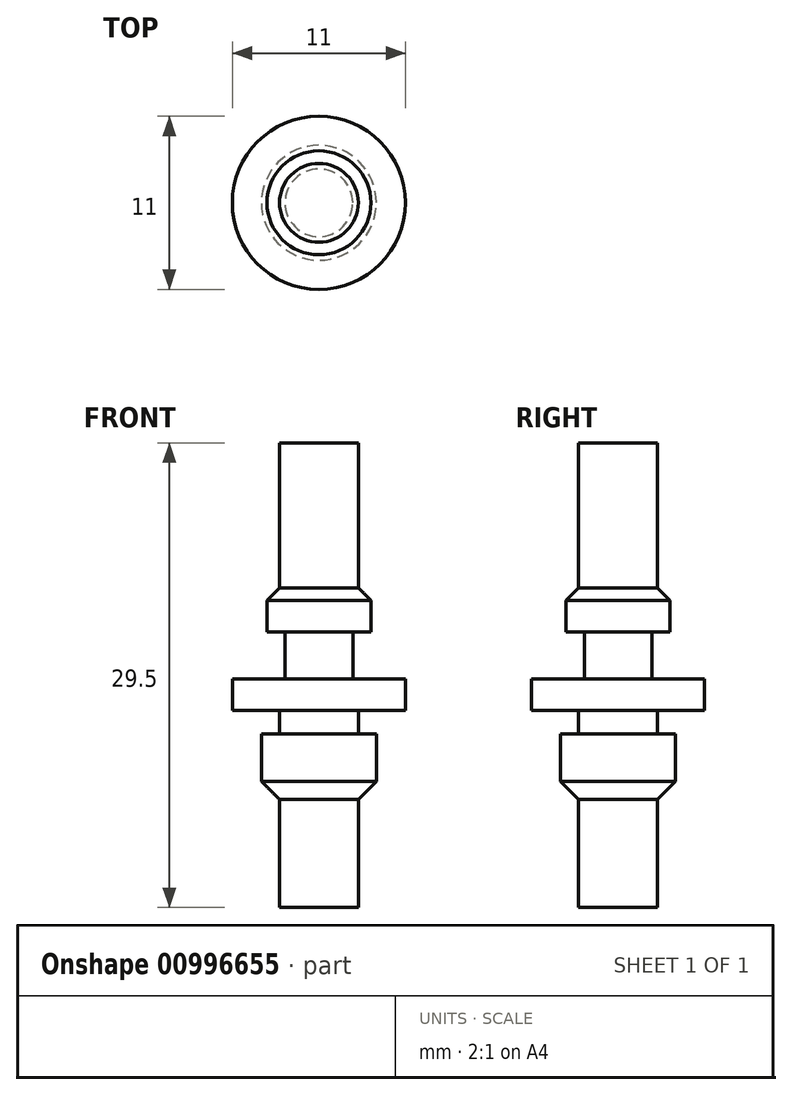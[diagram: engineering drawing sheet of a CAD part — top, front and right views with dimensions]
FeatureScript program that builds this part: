
annotation { "Feature Type Name" : "Feature", "Feature Type Description" : "" }
export const myFeature = defineFeature(function(context is Context, id is Id, definition is map)
    precondition{}
    {
        {
            var Q0;
            Q0=qCreatedBy(makeId("Top.planeOp"),FACE);
            var sketch = newSketch(context, id + "F0", { "sketchPlane" : qUnion([Q0])});
            skCircle(sketch, "E0", {"center": v(0, 0) * mm, "radius": 5.5 * mm});
            skSolve(sketch);
        }
        {
            var Q0;
            Q0 = qSketchRegion(id + "F0", true);
            extrude(context, id + "F1", {"entities" : qUnion([Q0]), "depth" : 2 * mm, "offsetDistance" : 25 * mm});
        }
        {
            var Q0;
            Q0=makeQuery(id+"F1.opExtrude","CAP_FACE",FACE,{"disambiguationData":[OSD([sQuery(id+"F0.wireOp",EDGE,"E0")])],"isStart":false});
            var sketch = newSketch(context, id + "F2", { "sketchPlane" : qUnion([Q0])});
            skCircle(sketch, "E1", {"center": v(0, 0) * mm, "radius": 2.15 * mm});
            skSolve(sketch);
        }
        {
            var Q0;
            Q0 = qSketchRegion(id + "F2", true);
            extrude(context, id + "F3", {"entities" : qUnion([Q0]), "operationType" : NewBodyOperationType.ADD, "depth" : 3 * mm, "offsetDistance" : 25 * mm});
        }
        {
            var Q0;
            Q0=makeQuery(id+"F3.opExtrude","CAP_FACE",FACE,{"disambiguationData":[OSD([sQuery(id+"F2.wireOp",EDGE,"E1")])],"isStart":false});
            var sketch = newSketch(context, id + "F4", { "sketchPlane" : qUnion([Q0])});
            skCircle(sketch, "E2", {"center": v(0, 0) * mm, "radius": 3.3 * mm});
            skSolve(sketch);
        }
        {
            var Q0;
            Q0 = qSketchRegion(id + "F4", true);
            extrude(context, id + "F5", {"entities" : qUnion([Q0]), "operationType" : NewBodyOperationType.ADD, "depth" : 12 * mm, "offsetDistance" : 25 * mm});
        }
        {
            var Q0;
            Q0=makeQuery(id+"F5.opExtrude","CAP_FACE",FACE,{"disambiguationData":[OSD([sQuery(id+"F4.wireOp",EDGE,"E2")])],"isStart":false});
            var sketch = newSketch(context, id + "F6", { "sketchPlane" : qUnion([Q0])});
            skCircle(sketch, "E3", {"center": v(0, 0) * mm, "radius": 2.5 * mm});
            skCircle(sketch, "E4", {"center": v(0, 0) * mm, "radius": 5 * mm});
            skSolve(sketch);
        }
        {
            var Q0;
            Q0 = qSketchRegion(id + "F6", true);
            extrude(context, id + "F7", {"entities" : qUnion([Q0]), "operationType" : NewBodyOperationType.REMOVE, "oppositeDirection" : true, "depth" : 7 * mm, "offsetDistance" : 25 * mm});
        }
        {
            var Q0;
            Q0=makeQuery(id+"F7.boolean.opBoolean","INTERSECT",EDGE,{"derivedFrom":[makeQuery(id+"F5.opExtrude","SWEPT_FACE",FACE,{"disambiguationData":[OSD([sQuery(id+"F4.wireOp",EDGE,"E2")])]}),makeQuery(id+"F7.opExtrude","CAP_FACE",FACE,{"disambiguationData":[OSD([sQuery(id+"F6.wireOp",EDGE,"E3"),sQuery(id+"F6.wireOp",EDGE,"E4")])],"isStart":false})]});
            chamfer(context, id + "F8", {"entities" : qUnion([Q0]), "width" : 3 * mm, "tangentPropagation" : true});
        }
        {
            var Q0;
            Q0=makeQuery(id+"F1.opExtrude","CAP_FACE",FACE,{"disambiguationData":[OSD([sQuery(id+"F0.wireOp",EDGE,"E0")])],"isStart":true});
            var sketch = newSketch(context, id + "F9", { "sketchPlane" : qUnion([Q0])});
            skCircle(sketch, "E5", {"center": v(0, 0) * mm, "radius": 2.5 * mm});
            skSolve(sketch);
        }
        {
            var Q0;
            Q0 = qSketchRegion(id + "F9", true);
            extrude(context, id + "F10", {"entities" : qUnion([Q0]), "operationType" : NewBodyOperationType.ADD, "depth" : 1.5 * mm, "offsetDistance" : 25 * mm});
        }
        {
            var Q0;
            Q0=makeQuery(id+"F10.opExtrude","CAP_FACE",FACE,{"disambiguationData":[OSD([sQuery(id+"F9.wireOp",EDGE,"E5")])],"isStart":false});
            var sketch = newSketch(context, id + "F11", { "sketchPlane" : qUnion([Q0])});
            skCircle(sketch, "E6", {"center": v(0, 0) * mm, "radius": 3.65 * mm});
            skSolve(sketch);
        }
        {
            var Q0;
            Q0 = qSketchRegion(id + "F11", true);
            extrude(context, id + "F12", {"entities" : qUnion([Q0]), "operationType" : NewBodyOperationType.ADD, "depth" : 11 * mm, "offsetDistance" : 25 * mm});
        }
        {
            var Q0;
            Q0=makeQuery(id+"F12.opExtrude","CAP_FACE",FACE,{"disambiguationData":[OSD([sQuery(id+"F11.wireOp",EDGE,"E6")])],"isStart":false});
            var sketch = newSketch(context, id + "F13", { "sketchPlane" : qUnion([Q0])});
            skCircle(sketch, "E7", {"center": v(0, 0) * mm, "radius": 2.5 * mm});
            skCircle(sketch, "E8", {"center": v(0, 0) * mm, "radius": 5 * mm});
            skSolve(sketch);
        }
        {
            var Q0;
            Q0 = qSketchRegion(id + "F13", true);
            extrude(context, id + "F14", {"entities" : qUnion([Q0]), "operationType" : NewBodyOperationType.REMOVE, "oppositeDirection" : true, "depth" : 5 * mm, "offsetDistance" : 25 * mm});
        }
        {
            var Q0;
            Q0=makeQuery(id+"F14.boolean.opBoolean","INTERSECT",EDGE,{"derivedFrom":[makeQuery(id+"F12.opExtrude","SWEPT_FACE",FACE,{"disambiguationData":[OSD([sQuery(id+"F11.wireOp",EDGE,"E6")])]}),makeQuery(id+"F14.opExtrude","CAP_FACE",FACE,{"disambiguationData":[OSD([sQuery(id+"F13.wireOp",EDGE,"E7"),sQuery(id+"F13.wireOp",EDGE,"E8")])],"isStart":false})]});
            chamfer(context, id + "F15", {"entities" : qUnion([Q0]), "width" : 3 * mm, "tangentPropagation" : true});
        }
    });
